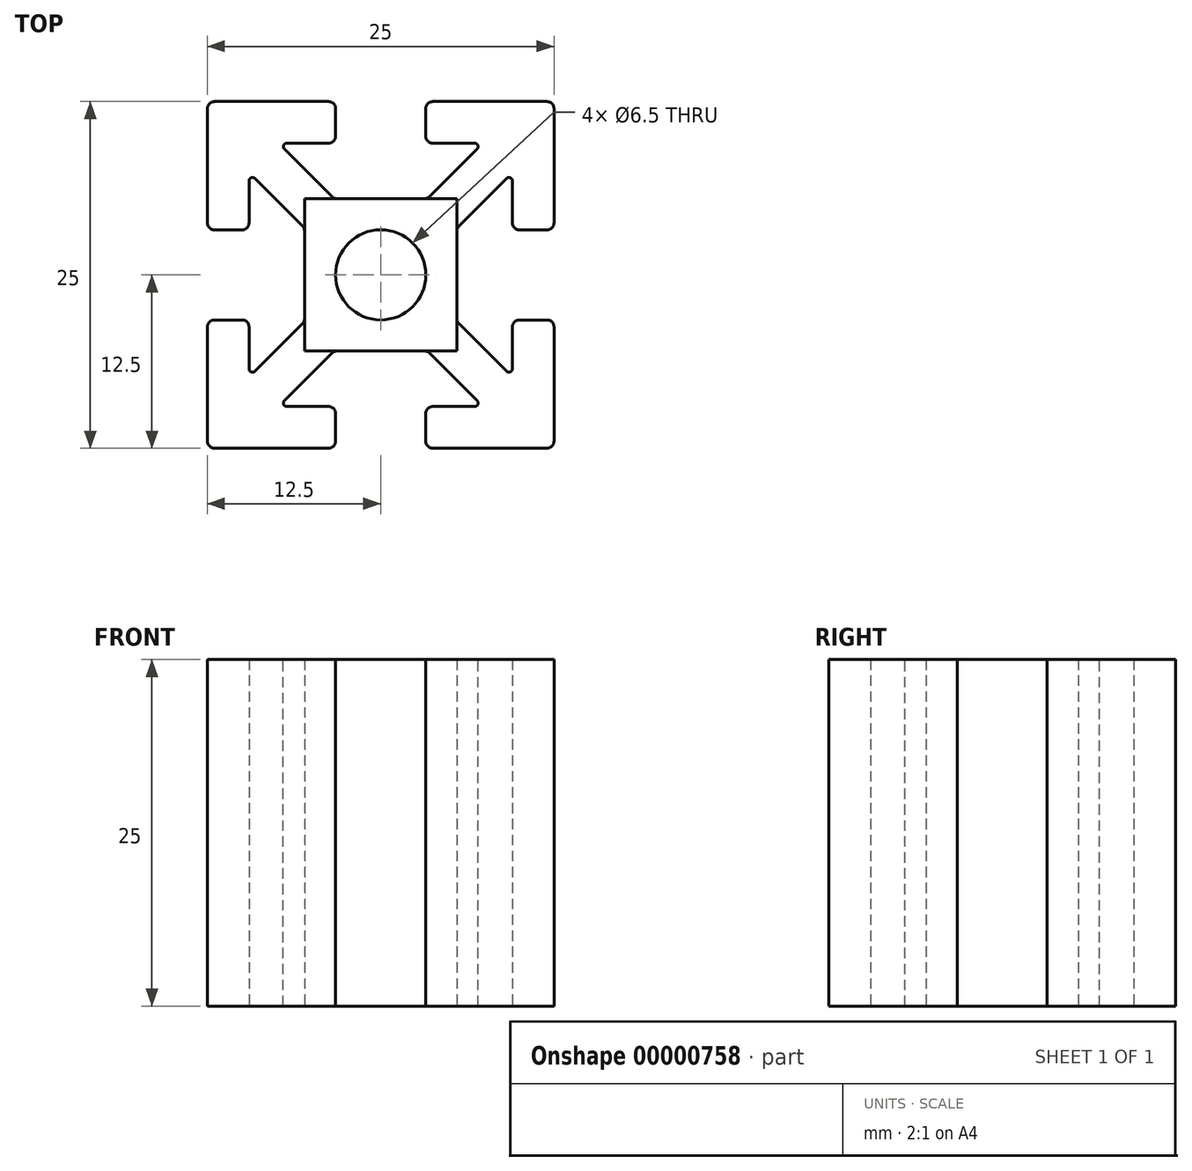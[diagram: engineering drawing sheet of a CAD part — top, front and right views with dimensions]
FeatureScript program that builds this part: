
annotation { "Feature Type Name" : "Feature", "Feature Type Description" : "" }
export const myFeature = defineFeature(function(context is Context, id is Id, definition is map)
    precondition{}
    {
        {
            var Q0;
            Q0=qCreatedBy(makeId("Top.planeOp"),FACE);
            var sketch = newSketch(context, id + "F0", { "sketchPlane" : qUnion([Q0])});
            skLineSegment(sketch, "E0.bottom", {"start": v(0, 0) * mm, "end": v(3.25, 0) * mm});
            skLineSegment(sketch, "E0.top", {"start": v(0, 12.5) * mm, "end": v(12.5, 12.5) * mm});
            skLineSegment(sketch, "E0.left", {"start": v(0, 0) * mm, "end": v(0, 3.25) * mm});
            skLineSegment(sketch, "E0.right", {"start": v(12.5, 0) * mm, "end": v(12.5, 12.5) * mm});
            skArc(sketch, "E1", {"start": v(0.98, 3.1) * mm, "mid": v(-2.3, -2.3) * mm, "end": v(3.1, 0.98) * mm});
            skLineSegment(sketch, "E2", {"start": v(2.3, 2.3) * mm, "end": v(12.5, 12.5) * mm});
            skLineSegment(sketch, "E3", {"start": v(0, 9.5) * mm, "end": v(7.38, 9.5) * mm});
            skLineSegment(sketch, "E4", {"start": v(7.38, 9.5) * mm, "end": v(0.98, 3.1) * mm});
            skLineSegment(sketch, "E5.0.MirrorCS", {"start": v(9.5, 7.38) * mm, "end": v(3.1, 0.98) * mm});
            skLineSegment(sketch, "E6.0.MirrorCS", {"start": v(9.5, 0) * mm, "end": v(9.5, 7.38) * mm});
            skPoint(sketch, "E7.orphan", {"position": v(2.12, 0) * mm});
            skPoint(sketch, "E8.orphan", {"position": v(0, 2.12) * mm});
            skLineSegment(sketch, "E9.trimOffspring", {"start": v(0, 9.5) * mm, "end": v(0, 12.5) * mm});
            skLineSegment(sketch, "E10.trimOffspring", {"start": v(9.5, 0) * mm, "end": v(12.5, 0) * mm});
            skLineSegment(sketch, "E11", {"start": v(3.25, 12.5) * mm, "end": v(3.25, 9.5) * mm});
            skLineSegment(sketch, "E12.0.MirrorCS", {"start": v(12.5, 3.25) * mm, "end": v(9.5, 3.25) * mm});
            skLineSegment(sketch, "E13.rect.bottom", {"start": v(5.5, 5.5) * mm, "end": v(-5.5, 5.5) * mm});
            skLineSegment(sketch, "E13.rect.top", {"start": v(5.5, -5.5) * mm, "end": v(-5.5, -5.5) * mm});
            skLineSegment(sketch, "E13.rect.left", {"start": v(5.5, 5.5) * mm, "end": v(5.5, -5.5) * mm});
            skLineSegment(sketch, "E13.rect.right", {"start": v(-5.5, 5.5) * mm, "end": v(-5.5, -5.5) * mm});
            skArc(sketch, "E14", {"start": v(3.1, 0.98) * mm, "mid": v(2.3, 2.3) * mm, "end": v(0.98, 3.1) * mm});
            skSolve(sketch);
        }
        {
            var Q0;
            {var subQ5=sQuery(id+"F0.wireOp",EDGE,"E11");Q0=makeQuery(id+"F0.imprint","IMPRINT",FACE,{"disambiguationData":[TD([[makeQuery(id+"F0.imprint","IMPRINT",EDGE,{"derivedFrom":subQ5}),1.0]])]});}
            var Q1;
            {var subQ6=sQuery(id+"F0.wireOp",EDGE,"E12.0.MirrorCS");Q1=makeQuery(id+"F0.imprint","IMPRINT",FACE,{"disambiguationData":[TD([[makeQuery(id+"F0.imprint","IMPRINT",EDGE,{"derivedFrom":subQ6}),-1.0]])]});}
            var Q2;
            {var subQ0=sQuery(id+"F0.wireOp",EDGE,"E14");var subQ1=sQuery(id+"F0.wireOp",EDGE,"E2");var subQ2=makeQuery(id+"F0.imprint","INTERSECT",VERTEX,{"derivedFrom":[subQ1,subQ0]});Q2=makeQuery(id+"F0.imprint","IMPRINT",FACE,{"disambiguationData":[TD([[makeQuery(id+"F0.imprint","IMPRINT",EDGE,{"disambiguationData":[TD([[subQ2,-1.0]])],"derivedFrom":subQ1}),1.0]])]});}
            var Q3;
            {var subQ0=sQuery(id+"F0.wireOp",EDGE,"E14");var subQ1=sQuery(id+"F0.wireOp",EDGE,"E2");var subQ2=makeQuery(id+"F0.imprint","INTERSECT",VERTEX,{"derivedFrom":[subQ1,subQ0]});Q3=makeQuery(id+"F0.imprint","IMPRINT",FACE,{"disambiguationData":[TD([[makeQuery(id+"F0.imprint","IMPRINT",EDGE,{"disambiguationData":[TD([[subQ2,-1.0]])],"derivedFrom":subQ1}),-1.0]])]});}
            var Q4;
            {var subQ4=sQuery(id+"F0.wireOp",EDGE,"E13.rect.top");Q4=makeQuery(id+"F0.imprint","IMPRINT",FACE,{"disambiguationData":[TD([[makeQuery(id+"F0.imprint","IMPRINT",EDGE,{"derivedFrom":subQ4}),-1.0]])]});}
            extrude(context, id + "F1", {"entities" : qUnion([Q0, Q1, Q2, Q3, Q4]), "endBound" : BoundingType.SYMMETRIC, "depth" : 25 * mm});
        }
        {
            var Q0;
            Q0=makeQuery(id+"F1.opExtrude","SWEPT_EDGE",EDGE,{"disambiguationData":[OSD([sQuery(id+"F0.wireOp",EDGE,"E3"),sQuery(id+"F0.wireOp",EDGE,"E11")])]});
            var Q1;
            Q1=makeQuery(id+"F1.opExtrude","SWEPT_EDGE",EDGE,{"disambiguationData":[OSD([sQuery(id+"F0.wireOp",EDGE,"E0.top"),sQuery(id+"F0.wireOp",EDGE,"E11")])]});
            var Q2;
            Q2=makeQuery(id+"F1.opExtrude","SWEPT_EDGE",EDGE,{"disambiguationData":[OSD([sQuery(id+"F0.wireOp",EDGE,"E0.right"),sQuery(id+"F0.wireOp",EDGE,"E12.0.MirrorCS")])]});
            var Q3;
            Q3=makeQuery(id+"F1.opExtrude","SWEPT_EDGE",EDGE,{"disambiguationData":[OSD([sQuery(id+"F0.wireOp",EDGE,"E6.0.MirrorCS"),sQuery(id+"F0.wireOp",EDGE,"E12.0.MirrorCS")])]});
            var Q4;
            Q4=makeQuery(id+"F1.opExtrude","SWEPT_EDGE",EDGE,{"disambiguationData":[OSD([sQuery(id+"F0.wireOp",EDGE,"E0.top"),sQuery(id+"F0.wireOp",EDGE,"E0.right"),sQuery(id+"F0.wireOp",EDGE,"E2")])]});
            var Q5;
            Q5=makeQuery(id+"F1.opExtrude","SWEPT_EDGE",EDGE,{"disambiguationData":[OSD([sQuery(id+"F0.wireOp",EDGE,"E5.0.MirrorCS"),sQuery(id+"F0.wireOp",EDGE,"E13.rect.left")])]});
            var Q6;
            Q6=makeQuery(id+"F1.opExtrude","SWEPT_EDGE",EDGE,{"disambiguationData":[OSD([sQuery(id+"F0.wireOp",EDGE,"E4"),sQuery(id+"F0.wireOp",EDGE,"E13.rect.bottom")])]});
            fillet(context, id + "F2", {"entities" : qUnion([Q0, Q1, Q2, Q3, Q4, Q5, Q6]), "radius" : .5 * mm, "tangentPropagation" : true, "allowEdgeOverflow" : false});
        }
        {
            var Q0;
            Q0=makeQuery(id+"F1.opExtrude","SWEPT_EDGE",EDGE,{"disambiguationData":[OSD([sQuery(id+"F0.wireOp",EDGE,"E5.0.MirrorCS"),sQuery(id+"F0.wireOp",EDGE,"E6.0.MirrorCS")])]});
            var Q1;
            Q1=makeQuery(id+"F1.opExtrude","SWEPT_EDGE",EDGE,{"disambiguationData":[OSD([sQuery(id+"F0.wireOp",EDGE,"E3"),sQuery(id+"F0.wireOp",EDGE,"E4")])]});
            fillet(context, id + "F3", {"entities" : qUnion([Q0, Q1]), "radius" : .25 * mm, "tangentPropagation" : true, "allowEdgeOverflow" : false});
        }
        {
            var Q0;
            Q0=makeQuery(id+"F1.opExtrude","SWEPT_BODY",BODY,{"disambiguationData":[OSD([sQuery(id+"F0.wireOp",EDGE,"E0.top"),sQuery(id+"F0.wireOp",EDGE,"E0.right"),sQuery(id+"F0.wireOp",EDGE,"E1"),sQuery(id+"F0.wireOp",EDGE,"E3"),sQuery(id+"F0.wireOp",EDGE,"E4"),sQuery(id+"F0.wireOp",EDGE,"E5.0.MirrorCS"),sQuery(id+"F0.wireOp",EDGE,"E6.0.MirrorCS"),sQuery(id+"F0.wireOp",EDGE,"E11"),sQuery(id+"F0.wireOp",EDGE,"E12.0.MirrorCS"),sQuery(id+"F0.wireOp",EDGE,"E13.rect.bottom"),sQuery(id+"F0.wireOp",EDGE,"E13.rect.top"),sQuery(id+"F0.wireOp",EDGE,"E13.rect.left"),sQuery(id+"F0.wireOp",EDGE,"E13.rect.right"),sQuery(id+"F0.wireOp",EDGE,"E14")])]});
            var Q1;
            Q1=makeQuery(id+"F1.opExtrude","CAP_EDGE",EDGE,{"disambiguationData":[OSD([sQuery(id+"F0.wireOp",EDGE,"E1"),sQuery(id+"F0.wireOp",EDGE,"E14")])],"isStart":false});
            circularPattern(context, id + "F4", {"entities" : qUnion([Q0]), "axis" : qUnion([Q1]), "angle" : 90 * degree, "instanceCount" : 4});
        }
    });
